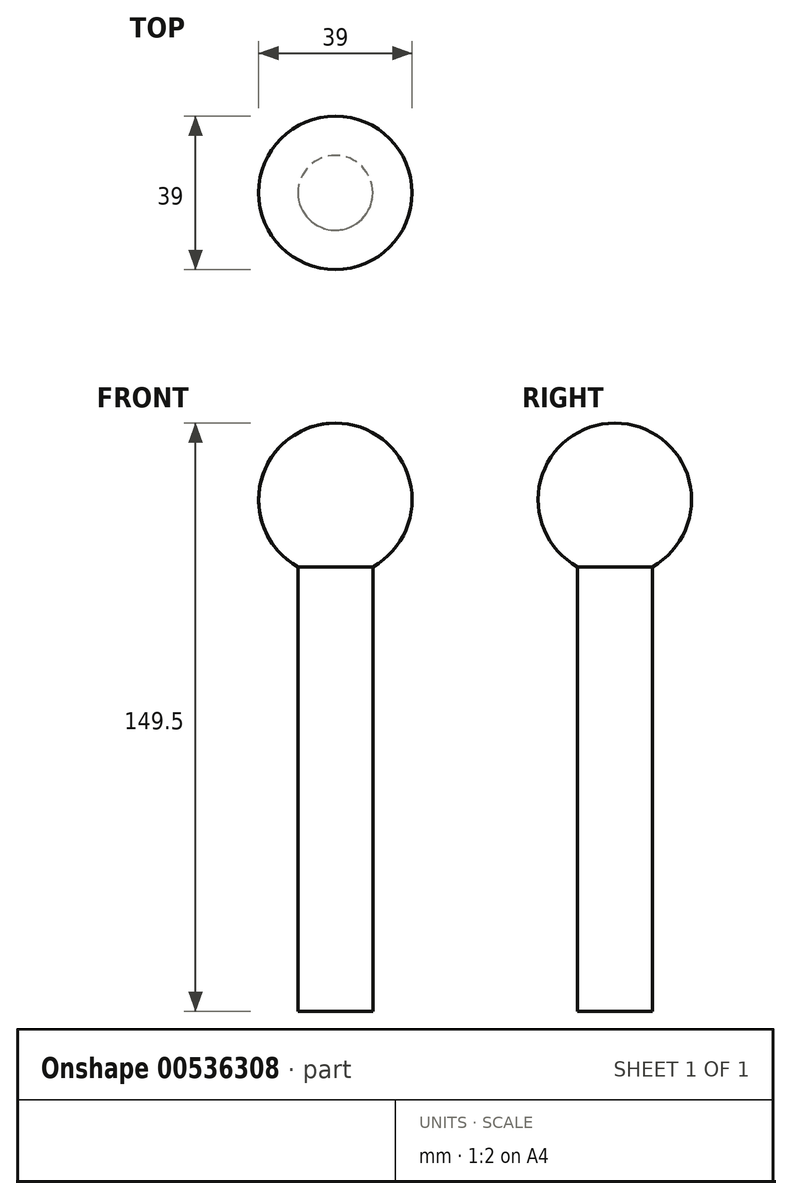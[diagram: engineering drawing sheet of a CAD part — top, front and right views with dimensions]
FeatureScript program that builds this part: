
annotation { "Feature Type Name" : "Feature", "Feature Type Description" : "" }
export const myFeature = defineFeature(function(context is Context, id is Id, definition is map)
    precondition{}
    {
        {
            var Q0;
            Q0=qCreatedBy(makeId("Front.planeOp"),FACE);
            var sketch = newSketch(context, id + "F0", { "sketchPlane" : qUnion([Q0])});
            skArc(sketch, "E0", {"start": v(0, -19.5) * mm, "mid": v(19.5, 0) * mm, "end": v(0, 19.5) * mm});
            skLineSegment(sketch, "E1", {"start": v(0, 19.5) * mm, "end": v(0, -19.5) * mm});
            skSolve(sketch);
        }
        {
            var Q0;
            Q0 = qSketchRegion(id + "F0", true);
            var Q1;
            Q1=sQuery(id+"F0.wireOp",EDGE,"E1");
            revolve(context, id + "F1", {"entities" : qUnion([Q0]), "axis" : qUnion([Q1]), "revolveType" : RevolveType.FULL});
        }
        {
            var Q0;
            Q0=qCreatedBy(makeId("Top.planeOp"),FACE);
            var sketch = newSketch(context, id + "F2", { "sketchPlane" : qUnion([Q0])});
            skCircle(sketch, "E2", {"center": v(0, 0) * mm, "radius": 9.5 * mm});
            skSolve(sketch);
        }
        {
            var Q0;
            Q0 = qSketchRegion(id + "F2", true);
            extrude(context, id + "F3", {"entities" : qUnion([Q0]), "operationType" : NewBodyOperationType.ADD, "oppositeDirection" : true, "depth" : 130 * mm, "offsetDistance" : 25 * mm});
        }
    });
